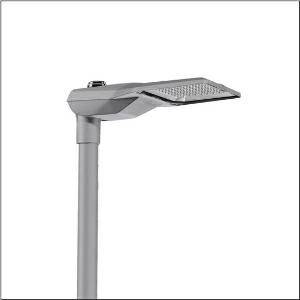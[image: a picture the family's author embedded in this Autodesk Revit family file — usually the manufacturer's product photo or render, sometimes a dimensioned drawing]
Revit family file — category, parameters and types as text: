
# Revit family: streetlight_sl_21_midi___st1_0a_5xe7d57n08mb_4ce1
name_source: partatom
category: Lighting Fixtures
units: mm (PartAtom-declared; Revit-internal decimal feet)

## family parameters
Cut with Voids When Loaded = No
Host = Face
Light Source = No
Part Type = Normal
Room Calculation Point = No
Round Connector Dimension = Use Diameter
Shared = No

## types (1)
- --- (1 x LED, 15800 lm, 137 W, 3000K)
    Apparent Load = 137 VA
    CIE Flux Codes = 37 72 97 100 100
    Color Rendering = 80
    Color Temperature = 3000K
    Default Elevation = 1800 mm
    Description = Streetlight SL 21 midi, mast luminaire, primary light control with lens, of PMMA, primary optical cover: cover, of toughened safety glass, transparent, light distribution: ST1.0a, light emission: direct distribution, primary light characteristic: asymmetric, installation type: side-entry, LED, 3G 2.5mm², High Power LED, rated luminous flux: 15.800lm, luminous efficacy: 115lm/W, light colour: 830, colour temperature: 3000K, control: overheat protection, pre-setting: linear dimming characteristic, constant luminous flux control, time-dependent luminous flux control, flexible luminous flux parameterisation, mains connection: 220..240V, AC, 50/60Hz, connection cable pre-assembled, cable length: 12,5m, wiring characteristics: H05VV-F, start of lifetime: 137W, end of service life: 144W, reduction: 61W, luminaire housing, of diecast aluminium (EN AC-44300), powder-coated, Siteco® metallic grey (DB 702S), corrosivity category C5 mid according to DIN EN ISO 12944, multi-level sealing system, sealing non-destructively replaceable, inclination adjustable: 0°, 5°, 10°, 15°, length: 644mm, width: 335mm, height: 110mm, spigot size: 42mm (side-entry), protection rating (complete): IP66, insulation class (complete): insulation class I (protective earthing), certification: CE, ENEC, ENEC+, VDE, impact resistance: IK09, permissible operating ambient temperature for outdoor applications: -40..+50°C, standard-compliant lighting for roads and squares, packaging unit: 1 piece

Light Distribution: ST1.0a
    Height = 111 mm
    Lamp = 1 x LED
    Lamp Light Flux = 15800 lm
    Lamp Power = 137 W
    Lamp count = 1
    Length = 644 mm
    Luminous efficacy = 115 lm/W
    Manufacturer = Siteco
    ModVariant = No
    Model = 5XE7D57N08MB
    Number of Poles = 1
    OnlyDefault = Yes
    Power Factor = 1
    Product Name = Streetlight SL 21 midi | ST1.0a
    Product group = mast luminaire | pylon top
    ProductGroupID = 6100
    Protection Class = Protection class I
    Protection Degree = IP 66
    RLX_Detail_Level = 1
    RLX_Emergency_Light_Flux = 0 lm
    RLX_Emergency_Type = 0
    RLX_Emergency_Type_DB = No
    RlxData = <blob elided: 91653 chars, md5=46a60a86>
    Socket = socket
    Standby Power = 0 W
    System Light Flux = 15800 lm
    System Power = 137 W
    Type Comments = factory setting: luminous flux: 100 % | dim-lin: 254 | 700 mA
    Type Image = l_1294377.jpg
    URL = http://relux.com
    VarID = @adj_105735
    Voltage = 0 V
    Weight = 0.00 kg
    Width = 336 mm

## geometry (parser evidence)
native form markers: Blend x4, Sweep x11
no freeform markers — native parametric forms only
